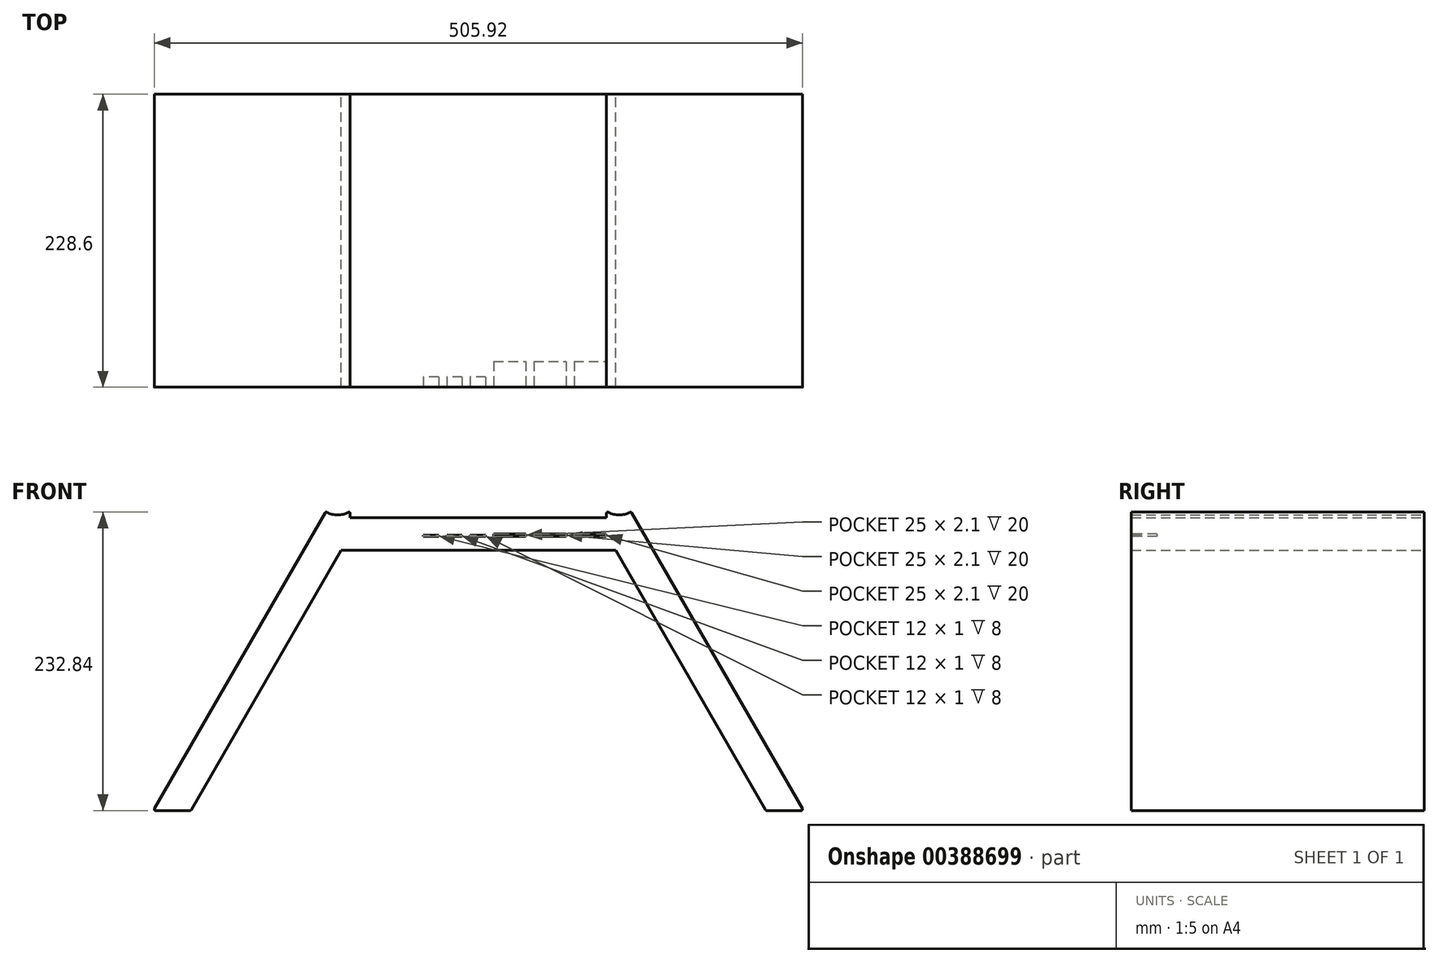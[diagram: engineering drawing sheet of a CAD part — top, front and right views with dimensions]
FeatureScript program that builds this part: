
annotation { "Feature Type Name" : "Feature", "Feature Type Description" : "" }
export const myFeature = defineFeature(function(context is Context, id is Id, definition is map)
    precondition{}
    {
        {
            var Q0;
            Q0=qCreatedBy(makeId("Front.planeOp"),FACE);
            var sketch = newSketch(context, id + "F0", { "sketchPlane" : qUnion([Q0])});
            skLineSegment(sketch, "E0", {"start": v(83.58, 53.49) * mm, "end": v(-38.13, 53.49) * mm});
            skLineSegment(sketch, "E1", {"start": v(-38.13, 53.49) * mm, "end": v(-170.11, -175.11) * mm});
            skLineSegment(sketch, "E2", {"start": v(-170.11, -175.11) * mm, "end": v(-140.78, -175.11) * mm});
            skLineSegment(sketch, "E3", {"start": v(-140.78, -175.11) * mm, "end": v(-23.47, 28.09) * mm});
            skLineSegment(sketch, "E4", {"start": v(-23.47, 28.09) * mm, "end": v(83.58, 28.09) * mm});
            skLineSegment(sketch, "E5", {"start": v(83.58, 28.09) * mm, "end": v(83.58, 53.49) * mm, "construction": true});
            skLineSegment(sketch, "E6.MirrorCS", {"start": v(307.94, -175.11) * mm, "end": v(190.63, 28.09) * mm});
            skLineSegment(sketch, "E7.MirrorCS", {"start": v(190.63, 28.09) * mm, "end": v(83.58, 28.09) * mm});
            skLineSegment(sketch, "E8.MirrorCS", {"start": v(83.58, 53.49) * mm, "end": v(205.29, 53.49) * mm});
            skLineSegment(sketch, "E9.MirrorCS", {"start": v(205.29, 53.49) * mm, "end": v(337.27, -175.11) * mm});
            skLineSegment(sketch, "E10.MirrorCS", {"start": v(337.27, -175.11) * mm, "end": v(307.94, -175.11) * mm});
            skLineSegment(sketch, "E11", {"start": v(-104.12, -60.81) * mm, "end": v(-82.13, -73.51) * mm, "construction": true});
            skLineSegment(sketch, "E12", {"start": v(-16.42, 53.49) * mm, "end": v(-16.42, 58.49) * mm});
            skLineSegment(sketch, "E13", {"start": v(-35.47, 58.1) * mm, "end": v(-38.13, 53.49) * mm});
            skArc(sketch, "E14", {"start": v(-35.47, 58.1) * mm, "mid": v(-25.89, 55.49) * mm, "end": v(-16.42, 58.49) * mm});
            skLineSegment(sketch, "E15.MirrorCS", {"start": v(183.58, 53.49) * mm, "end": v(183.58, 58.49) * mm});
            skLineSegment(sketch, "E16.MirrorCS", {"start": v(202.63, 58.1) * mm, "end": v(205.29, 53.49) * mm});
            skArc(sketch, "E17.MirrorCS", {"start": v(202.63, 58.1) * mm, "mid": v(193.05, 55.49) * mm, "end": v(183.58, 58.49) * mm});
            skSolve(sketch);
        }
        {
            var Q0;
            Q0 = qSketchRegion(id + "F0", true);
            extrude(context, id + "F1", {"entities" : qUnion([Q0]), "depth" : 228.6 * mm});
        }
        {
            var Q0;
            Q0=makeQuery(id+"F1.opExtrude","SWEPT_EDGE",EDGE,{"disambiguationData":[OSD([sQuery(id+"F0.wireOp",EDGE,"E13"),sQuery(id+"F0.wireOp",EDGE,"E14")])]});
            var Q1;
            Q1=makeQuery(id+"F1.opExtrude","SWEPT_EDGE",EDGE,{"disambiguationData":[OSD([sQuery(id+"F0.wireOp",EDGE,"E12"),sQuery(id+"F0.wireOp",EDGE,"E14")])]});
            var Q2;
            Q2=makeQuery(id+"F1.opExtrude","SWEPT_EDGE",EDGE,{"disambiguationData":[OSD([sQuery(id+"F0.wireOp",EDGE,"E15.MirrorCS"),sQuery(id+"F0.wireOp",EDGE,"E17.MirrorCS")])]});
            var Q3;
            Q3=makeQuery(id+"F1.opExtrude","SWEPT_EDGE",EDGE,{"disambiguationData":[OSD([sQuery(id+"F0.wireOp",EDGE,"E16.MirrorCS"),sQuery(id+"F0.wireOp",EDGE,"E17.MirrorCS")])]});
            var Q4;
            Q4=makeQuery(id+"F1.opExtrude","SWEPT_EDGE",EDGE,{"disambiguationData":[OSD([sQuery(id+"F0.wireOp",EDGE,"E1"),sQuery(id+"F0.wireOp",EDGE,"E2")])]});
            var Q5;
            Q5=makeQuery(id+"F1.opExtrude","SWEPT_EDGE",EDGE,{"disambiguationData":[OSD([sQuery(id+"F0.wireOp",EDGE,"E2"),sQuery(id+"F0.wireOp",EDGE,"E3")])]});
            var Q6;
            Q6=makeQuery(id+"F1.opExtrude","SWEPT_EDGE",EDGE,{"disambiguationData":[OSD([sQuery(id+"F0.wireOp",EDGE,"E6.MirrorCS"),sQuery(id+"F0.wireOp",EDGE,"E10.MirrorCS")])]});
            var Q7;
            Q7=makeQuery(id+"F1.opExtrude","SWEPT_EDGE",EDGE,{"disambiguationData":[OSD([sQuery(id+"F0.wireOp",EDGE,"E9.MirrorCS"),sQuery(id+"F0.wireOp",EDGE,"E10.MirrorCS")])]});
            fillet(context, id + "F2", {"entities" : qUnion([Q0, Q1, Q2, Q3, Q4, Q5, Q6, Q7]), "radius" : 1 * mm, "tangentPropagation" : true, "allowEdgeOverflow" : false});
        }
        {
            var Q0;
            Q0=makeQuery(id+"F1.opExtrude","CAP_FACE",FACE,{"disambiguationData":[OSD([sQuery(id+"F0.wireOp",EDGE,"E0"),sQuery(id+"F0.wireOp",EDGE,"E1"),sQuery(id+"F0.wireOp",EDGE,"E2"),sQuery(id+"F0.wireOp",EDGE,"E3"),sQuery(id+"F0.wireOp",EDGE,"E4"),sQuery(id+"F0.wireOp",EDGE,"E6.MirrorCS"),sQuery(id+"F0.wireOp",EDGE,"E7.MirrorCS"),sQuery(id+"F0.wireOp",EDGE,"E8.MirrorCS"),sQuery(id+"F0.wireOp",EDGE,"E9.MirrorCS"),sQuery(id+"F0.wireOp",EDGE,"E10.MirrorCS"),sQuery(id+"F0.wireOp",EDGE,"E12"),sQuery(id+"F0.wireOp",EDGE,"E13"),sQuery(id+"F0.wireOp",EDGE,"E14"),sQuery(id+"F0.wireOp",EDGE,"E15.MirrorCS"),sQuery(id+"F0.wireOp",EDGE,"E16.MirrorCS"),sQuery(id+"F0.wireOp",EDGE,"E17.MirrorCS")])],"isStart":false});
            var sketch = newSketch(context, id + "F3", { "sketchPlane" : qUnion([Q0])});
            skLineSegment(sketch, "E18.bottom", {"start": v(158.3, 40.79) * mm, "end": v(183.3, 40.79) * mm});
            skLineSegment(sketch, "E18.top", {"start": v(158.3, 38.69) * mm, "end": v(183.3, 38.69) * mm});
            skLineSegment(sketch, "E18.left", {"start": v(158.3, 40.79) * mm, "end": v(158.3, 38.69) * mm});
            skLineSegment(sketch, "E18.right", {"start": v(183.3, 40.79) * mm, "end": v(183.3, 38.69) * mm});
            skLineSegment(sketch, "E19.bottom", {"start": v(126.94, 40.79) * mm, "end": v(151.94, 40.79) * mm});
            skLineSegment(sketch, "E19.top", {"start": v(126.94, 38.69) * mm, "end": v(151.94, 38.69) * mm});
            skLineSegment(sketch, "E19.left", {"start": v(126.94, 40.79) * mm, "end": v(126.94, 38.69) * mm});
            skLineSegment(sketch, "E19.right", {"start": v(151.94, 40.79) * mm, "end": v(151.94, 38.69) * mm});
            skLineSegment(sketch, "E20.bottom", {"start": v(95.6, 40.79) * mm, "end": v(120.6, 40.79) * mm});
            skLineSegment(sketch, "E20.top", {"start": v(95.6, 38.69) * mm, "end": v(120.6, 38.69) * mm});
            skLineSegment(sketch, "E20.left", {"start": v(95.6, 40.79) * mm, "end": v(95.6, 38.69) * mm});
            skLineSegment(sketch, "E20.right", {"start": v(120.6, 40.79) * mm, "end": v(120.6, 38.69) * mm});
            skSolve(sketch);
        }
        {
            var Q0;
            Q0=makeQuery(id+"F3.imprint","IMPRINT",FACE,{"disambiguationData":[TD([[makeQuery(id+"F3.imprint","IMPRINT",EDGE,{"derivedFrom":sQuery(id+"F3.wireOp",EDGE,"E18.bottom")}),-1.0]])]});
            var Q1;
            Q1=makeQuery(id+"F3.imprint","IMPRINT",FACE,{"disambiguationData":[TD([[makeQuery(id+"F3.imprint","IMPRINT",EDGE,{"derivedFrom":sQuery(id+"F3.wireOp",EDGE,"E19.bottom")}),-1.0]])]});
            var Q2;
            Q2=makeQuery(id+"F3.imprint","IMPRINT",FACE,{"disambiguationData":[TD([[makeQuery(id+"F3.imprint","IMPRINT",EDGE,{"derivedFrom":sQuery(id+"F3.wireOp",EDGE,"E20.bottom")}),-1.0]])]});
            var Q3;
            Q3=sQuery(id+"F3.wireOp",EDGE,"E20.bottom");
            var Q4;
            Q4=sQuery(id+"F3.wireOp",EDGE,"E19.top");
            var Q5;
            Q5=sQuery(id+"F3.wireOp",EDGE,"E18.bottom");
            var Q6;
            Q6=sQuery(id+"F3.wireOp",EDGE,"E18.top");
            var Q7;
            Q7=sQuery(id+"F3.wireOp",EDGE,"E19.bottom");
            var Q8;
            Q8=sQuery(id+"F3.wireOp",EDGE,"E20.top");
            var Q9;
            Q9=sQuery(id+"F3.wireOp",EDGE,"E19.left");
            var Q10;
            Q10=sQuery(id+"F3.wireOp",EDGE,"E19.right");
            var Q11;
            Q11=sQuery(id+"F3.wireOp",EDGE,"E18.left");
            var Q12;
            Q12=sQuery(id+"F3.wireOp",EDGE,"E18.right");
            var Q13;
            Q13=sQuery(id+"F3.wireOp",EDGE,"E20.left");
            var Q14;
            Q14=sQuery(id+"F3.wireOp",EDGE,"E20.right");
            extrude(context, id + "F4", {"entities" : qUnion([Q0, Q1, Q2]), "operationType" : NewBodyOperationType.REMOVE, "surfaceEntities" : qUnion([Q3, Q4, Q5, Q6, Q7, Q8, Q9, Q10, Q11, Q12, Q13, Q14]), "oppositeDirection" : true, "depth" : 20 * mm});
        }
        {
            var Q0;
            Q0=makeQuery(id+"F1.opExtrude","CAP_FACE",FACE,{"disambiguationData":[OSD([sQuery(id+"F0.wireOp",EDGE,"E0"),sQuery(id+"F0.wireOp",EDGE,"E1"),sQuery(id+"F0.wireOp",EDGE,"E2"),sQuery(id+"F0.wireOp",EDGE,"E3"),sQuery(id+"F0.wireOp",EDGE,"E4"),sQuery(id+"F0.wireOp",EDGE,"E6.MirrorCS"),sQuery(id+"F0.wireOp",EDGE,"E7.MirrorCS"),sQuery(id+"F0.wireOp",EDGE,"E8.MirrorCS"),sQuery(id+"F0.wireOp",EDGE,"E9.MirrorCS"),sQuery(id+"F0.wireOp",EDGE,"E10.MirrorCS"),sQuery(id+"F0.wireOp",EDGE,"E12"),sQuery(id+"F0.wireOp",EDGE,"E13"),sQuery(id+"F0.wireOp",EDGE,"E14"),sQuery(id+"F0.wireOp",EDGE,"E15.MirrorCS"),sQuery(id+"F0.wireOp",EDGE,"E16.MirrorCS"),sQuery(id+"F0.wireOp",EDGE,"E17.MirrorCS")])],"isStart":false});
            var sketch = newSketch(context, id + "F5", { "sketchPlane" : qUnion([Q0])});
            skLineSegment(sketch, "E21.bottom", {"start": v(89.24, 38.69) * mm, "end": v(77.24, 38.69) * mm});
            skLineSegment(sketch, "E21.top", {"start": v(89.24, 39.69) * mm, "end": v(77.24, 39.69) * mm});
            skLineSegment(sketch, "E21.left", {"start": v(89.24, 38.69) * mm, "end": v(89.24, 39.69) * mm});
            skLineSegment(sketch, "E21.right", {"start": v(77.24, 38.69) * mm, "end": v(77.24, 39.69) * mm});
            skLineSegment(sketch, "E22.bottom", {"start": v(70.9, 38.69) * mm, "end": v(58.9, 38.69) * mm});
            skLineSegment(sketch, "E22.top", {"start": v(70.9, 39.69) * mm, "end": v(58.9, 39.69) * mm});
            skLineSegment(sketch, "E22.left", {"start": v(70.9, 38.69) * mm, "end": v(70.9, 39.69) * mm});
            skLineSegment(sketch, "E22.right", {"start": v(58.9, 38.69) * mm, "end": v(58.9, 39.69) * mm});
            skLineSegment(sketch, "E23", {"start": v(77.24, 39.69) * mm, "end": v(77.24, 53.49) * mm, "construction": true});
            skLineSegment(sketch, "E24", {"start": v(70.9, 39.69) * mm, "end": v(70.9, 53.49) * mm, "construction": true});
            skPoint(sketch, "E25.oppositeSnap0", {"position": v(64.9, 39.69) * mm});
            skLineSegment(sketch, "E25.bottom", {"start": v(52.54, 38.69) * mm, "end": v(40.54, 38.69) * mm});
            skLineSegment(sketch, "E25.top", {"start": v(52.54, 39.69) * mm, "end": v(40.54, 39.69) * mm});
            skLineSegment(sketch, "E25.left", {"start": v(52.54, 38.69) * mm, "end": v(52.54, 39.69) * mm});
            skLineSegment(sketch, "E25.right", {"start": v(40.54, 38.69) * mm, "end": v(40.54, 39.69) * mm});
            skSolve(sketch);
        }
        {
            var Q0;
            Q0=makeQuery(id+"F5.imprint","IMPRINT",FACE,{"disambiguationData":[TD([[makeQuery(id+"F5.imprint","IMPRINT",EDGE,{"derivedFrom":sQuery(id+"F5.wireOp",EDGE,"E21.bottom")}),-1.0]])]});
            var Q1;
            Q1=makeQuery(id+"F5.imprint","IMPRINT",FACE,{"disambiguationData":[TD([[makeQuery(id+"F5.imprint","IMPRINT",EDGE,{"derivedFrom":sQuery(id+"F5.wireOp",EDGE,"E22.bottom")}),-1.0]])]});
            var Q2;
            Q2=makeQuery(id+"F5.imprint","IMPRINT",FACE,{"disambiguationData":[TD([[makeQuery(id+"F5.imprint","IMPRINT",EDGE,{"derivedFrom":sQuery(id+"F5.wireOp",EDGE,"E25.bottom")}),-1.0]])]});
            extrude(context, id + "F6", {"entities" : qUnion([Q0, Q1, Q2]), "operationType" : NewBodyOperationType.REMOVE, "oppositeDirection" : true, "depth" : 8 * mm});
        }
    });
